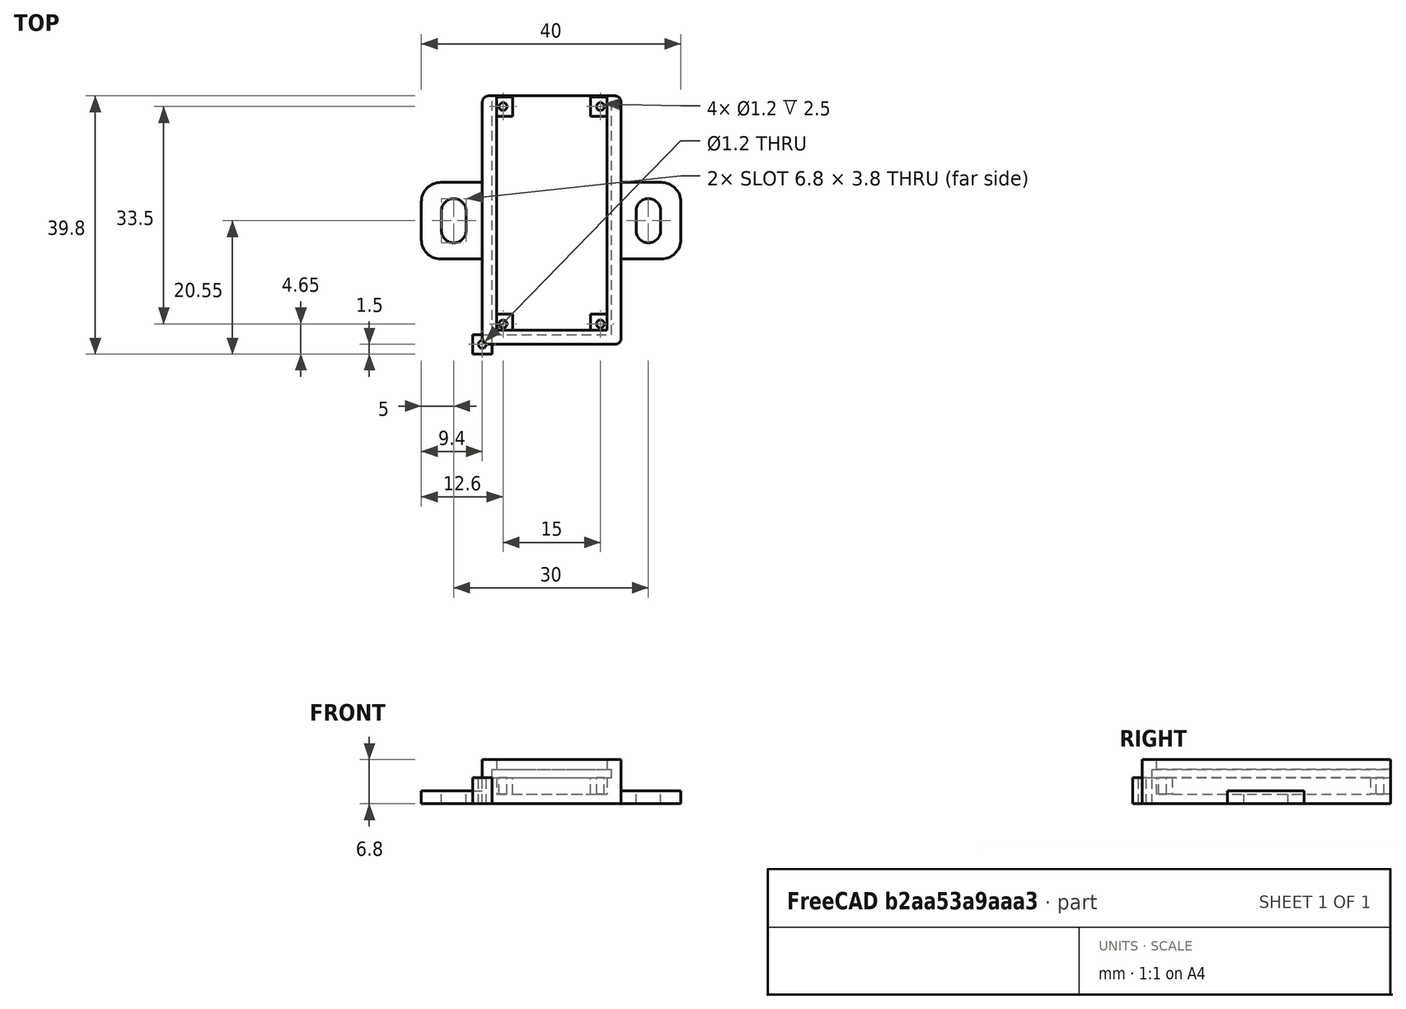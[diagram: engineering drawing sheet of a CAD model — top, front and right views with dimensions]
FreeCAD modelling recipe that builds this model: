
FCSTD DOCUMENT  (FreeCAD 0.19R23578 (Git))
Label: radar
License: FreeArt
LicenseURL: http://artlibre.org/licence/lal
objects: Part::Box×4, Part::MultiFuse×3, Part::Cut×2, Spreadsheet::Sheet×1, Part::Fillet×1, Part::Cylinder×1, Part::FeaturePython×1, Part::Feature×1, App::Part×1
note: 12 computed .brp shape members not serialized (recipe doc carries the construction recipe); baked Part::Feature solids carry a one-line shape summary decoded from their .brp

FEATURE [Spreadsheet::Sheet] Spreadsheet  label="p"
  cells = A1=pcb_x; B1(pcb_x)=18.4; A2=pcb_y; B2(pcb_y)=36.8; A3=pcb_z; B3(pcb_z)=1.3; A4=pcb_under; B4(pcb_under)=2.5; A5=side_wall; B5(side_wall)=1.5; A6=pcb_side_lane; B6(pcb_side_lane)=0.7; A7=bottom_wall; B7(bottom_wall)=1.5; A8=pcb_above; B8(pcb_above)=1.5; A9=hole_dist_x; B9(hole_dist_x)=15; A10=hole_dist_y; B10(hole_dist_y)=33.5; A11=hole_r; B11(hole_r)=0.6; A12=hole_stand_size; B12(hole_stand_size)=3
FEATURE [Part::Box] Box  label="external cube"
  AttacherType = Attacher::AttachEngine3D
  Height = 6.8
  Length = 21.4
  Width = 38.3
  expr: Length = <<p>>.pcb_x + 2 * <<p>>.side_wall
  expr: Width = <<p>>.pcb_y + <<p>>.side_wall
  expr: Height = <<p>>.bottom_wall + <<p>>.pcb_under + <<p>>.pcb_z + <<p>>.pcb_above
FEATURE [Part::Box] Box006  label="internal cube"
  AttacherType = Attacher::AttachEngine3D
  Height = 5.3
  Length = 17
  Placement = pos=(2.2,2.2,1.5) rot=(0,0,1;0rad)
  Width = 36.9
  expr: Length = <<p>>.pcb_x - 2 * <<p>>.pcb_side_lane
  expr: Width = <<p>>.pcb_y - 2 * <<p>>.pcb_side_lane + <<p>>.side_wall
  expr: Height = <<p>>.pcb_under + <<p>>.pcb_z + <<p>>.pcb_above
  expr: .Placement.Base.z = <<p>>.bottom_wall
  expr: .Placement.Base.x = <<p>>.side_wall + <<p>>.pcb_side_lane
  expr: .Placement.Base.y = <<p>>.side_wall + <<p>>.pcb_side_lane
FEATURE [Part::Box] Box007  label="pcb extract cube"
  AttacherType = Attacher::AttachEngine3D
  Height = 1.3
  Length = 18.4
  Placement = pos=(1.5,1.5,4) rot=(0,0,1;0rad)
  Width = 36.8
  expr: Height = <<p>>.pcb_z
  expr: .Placement.Base.z = <<p>>.bottom_wall + <<p>>.pcb_under
  expr: Width = <<p>>.pcb_y
  expr: Length = <<p>>.pcb_x
  expr: .Placement.Base.x = <<p>>.side_wall
  expr: .Placement.Base.y = <<p>>.side_wall
FEATURE [Part::MultiFuse] Fusion  label="extract fusion"
  Shapes = -> [Box006,Box007]
FEATURE [Part::Fillet] Fillet  label="external fillet"
  Base = -> Box
  Edges = 4 edges r=1: [Edge1,Edge3,Edge5,Edge7]
FEATURE [Part::Cylinder] Cylinder  label="hole"
  Angle = 360
  AttacherType = Attacher::AttachEngine3D
  Height = 10
  Radius = 0.6
  expr: Radius = <<p>>.hole_r
FEATURE [Part::Box] Box008  label="stand"
  AttacherType = Attacher::AttachEngine3D
  Height = 4
  Length = 3
  Placement = pos=(-1.5,-1.5,0) rot=(0,0,1;0rad)
  Width = 3
  expr: .Placement.Base.y = -<<p>>.hole_stand_size / 2
  expr: .Placement.Base.x = -<<p>>.hole_stand_size / 2
  expr: Width = <<p>>.hole_stand_size
  expr: Length = <<p>>.hole_stand_size
  expr: Height = <<p>>.pcb_under + <<p>>.bottom_wall
FEATURE [Part::Cut] Cut003002  label="stand hole cut"
  Base = -> Box008
  Tool = -> Cylinder
FEATURE [Part::FeaturePython] Array  label="hole array"  # Draft array (typed FeaturePython)
  Angle = 360
  ArrayType = 0
  Axis = (0,0,1)
  Base = -> Cut003002
  Center = (0,0,0)
  Count = 4
  ExpandArray = false
  Fuse = false
  IntervalAxis = (0,0,0)
  IntervalX = (15,0,0)
  IntervalY = (0,33.5,0)
  IntervalZ = (0,0,100)
  NumberCircles = 3
  NumberPolar = 5
  NumberX = 2
  NumberY = 2
  NumberZ = 1
  Placement = pos=(3.2,3.15,0) rot=(0,0,1;0rad)
  PlacementList = 4 placements: [(0,0,0),(0,33.5,0),(15,0,0),(15,33.5,0)]
  RadialDistance = 50
  ScaleList = (4) [(1,1,1),(1,1,1),(1,1,1),(1,1,1)]
  Symmetry = 1
  TangentialDistance = 25
  expr: .IntervalY.y = <<p>>.hole_dist_y
  expr: .Placement.Base.x = (2 * <<p>>.side_wall + <<p>>.pcb_x - <<p>>.hole_dist_x) / 2
  expr: .Placement.Base.y = (2 * <<p>>.side_wall + <<p>>.pcb_y - <<p>>.hole_dist_y) / 2
  expr: .IntervalX.x = <<p>>.hole_dist_x
FEATURE [Part::Feature] Cut003001  label="attach plane x dir001"
  Placement = pos=(-9.4,13.15,0) rot=(0,0,1;0rad)
  shape: bbox 40 x 11.8 x 2 mm, 18 faces (baked)
FEATURE [Part::MultiFuse] Fusion001  label="body fusion"
  Shapes = -> [Fillet,Cut003001]
FEATURE [Part::Cut] Cut  label="body cut"
  Base = -> Fusion001
  Tool = -> Fusion
FEATURE [Part::MultiFuse] Fusion002  label="radar fusion"
  Shapes = -> [Array,Cut]
FEATURE [App::Part] Part  label="radar pcb box part"
  Group = -> [Box,Fillet,Fusion001,Fusion,Box007,Box006,Cut,Cylinder,Box008,Cut003002,Array,Fusion002]
  Origin = -> Origin
